# Revit family: Maxlogic sirène,flasheur,Sirène avec Flasheur (Haut IP)
name_source: partatom
category: Fire Alarm Devices
units: mm (PartAtom-declared; Revit-internal decimal feet)

## family parameters
Cut with Voids When Loaded = No
Host = Face
Maintain Annotation Orientation = Yes
OmniClass Number = 23.85.30.21
OmniClass Title = Environmental Detection/Registration
Part Type = Normal
Room Calculation Point = No
Round Connector Dimension = Use Diameter
Shared = No

## types (9) — shared parameters
Adresse ligne 1 = Şerifali Mahallesi Kutup Sokak No:27/1-2-4 Ümraniye TR-34775 İSTANBUL
Couleur = Rouge
Deuxime Matèriel = Plastique
Durée de la garantie Travail = 2
Durée de la garantie réservé = 2
Hauteur Nominale = 122 mm
Longeur Nominale = 122 mm
Manuel d'installation = https://mavilielektronik.com
Manufacturer = Mavili Elektronik Ticaret A.Ş.
Model = MaxLogic
Numèro de Fax = (+)90 216 466 45 10
Tempèrature de Fonctionnement = (-10°C) - (+55°C)
URL = https://www.mavili.com.tr
Voltage de fonctionnement (default) = 24 V/DC
protection de Classe = IP21C
zero-valued in all types: Cost, Default Elevation

## per-type parameters (varying)
| type | Balıse | Charger adresse d'appareil | Code de  Performance | Code de Produit | Description | Hauteur de Montage | Largeur Nominale | Matériel Principe | Numéro de pose des travaux publics | Poids | Surface de Montage | Unité de durée de garantie | voltage fonction d'opération |
| Sirène Electronique Conventionnel | No |  | EN 54-3 | ML-2410 | Sirène Electronique Conventionnel | Hauteur  2,4 m  du Sol | 90 mm | Plastique Rouge ABS | 833-590 | 195 gr. | Montage à Mur | Ans | 21-28 V/DC |
| Flasheur Conventionnel | Yes |  | EN 54-23 | ML-2420 | Flasheur Conventionnel | Hauteur 2,4 m du Sol | 101,5 mm | Plastique Rouge ABS | 833-591 | 205 gr. | Montage à Mur | Year | 21-28 V/DC |
| Sirène avec Flash Electronique Conventionel | Yes |  | EN 54-3 / EN 54-23 | ML-2430 | Sirène avec Flash Electronique Conventionel | Hauteur 2,4 m du Sol | 101,5 mm | Plastique Rouge  ABS | 833-592 | 220 gr. | Montage à Mur | Ans | 21-28 V/DC |
| Sirène Adressable Electronique | No | Appareil adressage à Main | EN 54-3 | ML-1410 | Sirène Adressable Electronique | hauteur  2,4 m du sol | 90 mm | Plastique Rouge ABS |  | 186 gr. | Montage à mur | Ans | 18-33 V/DC |
| Sirène Adressable Electronique avec Isolateur de Court-Circuit | No | Appareil Adressage à Main | EN 54-3 | ML-1410.SCI | Sirène Adressable Electronique avec Isolateur de Court-Circuit | Hauteur  2,4 m du sol | 90 mm | Plastique Rouge ABS |  | 186 gr. | Montage à Mur | ANS | 18-33 V/DC |
| Flasheur Adressable | Yes | Appareil Adressage à Main | EN 54-23 | ML-1420 | Flasheur  Adressable | Zeminden 2,4 m yukarıda | 90 mm | Plastique Rouge  ABS |  | 201 gr. | Montage à Mur | Ans | 18-33 V/DC |
| Flasheur Adressable avec Isolateur de Court Circuit | Yes | Appareil adressage à main | EN 54-23 | ML-1420.SCI | Flasheur Adressable avec Isolateur de Court Circuit | Haut de   2,4 m du sol | 90 mm | Plastique Rouge ABS |  | 201 gr. | Montage à Mur | Ans | 18-33 V/DC |
| Sirène avec Flasheur Electronique adressable | Yes | Appareil Adressage à Main | EN 54-3 / EN 54-23 | ML-1430 | Sirène avec Flasheur Electronique adressable | Hauteur  2,4 m du sol | 90 mm | Plastique Rouge ABS |  | 217 gr. | Montage à Mur | Ans | 18-33 V/DC |
| Sirène avec Flash Electronique Adressable | Yes | Appareil adressage à main | EN 54-3 / EN 54-23 | ML-1430.SCI | Sirène avec Flash Electronique Adressable | Hauteur  2,4 m du Sol | 90 mm | Plastique Rouge ABS |  | 217 gr. | Montage à Mur | Ans | 18-33 V/DC |

## geometry (parser evidence)
native form markers: Sweep x5
no freeform markers — native parametric forms only
